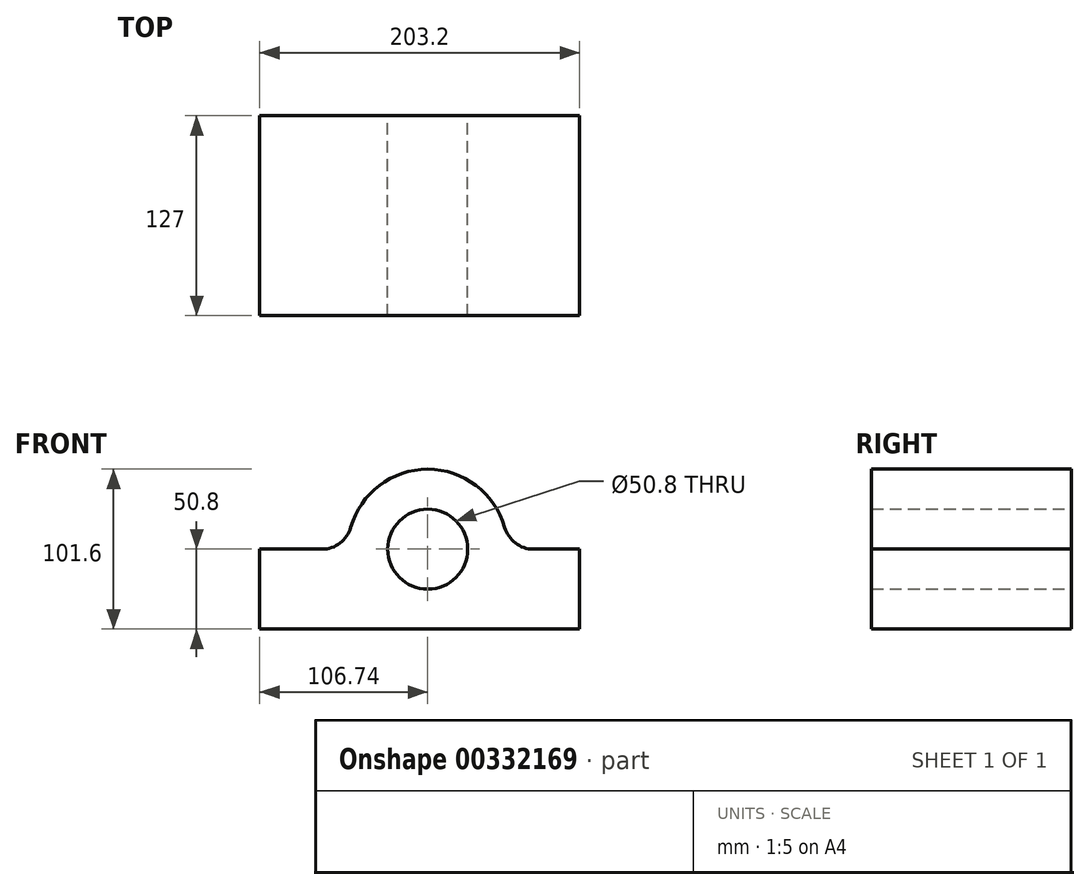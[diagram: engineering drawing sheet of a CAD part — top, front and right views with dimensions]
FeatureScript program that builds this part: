
annotation { "Feature Type Name" : "Feature", "Feature Type Description" : "" }
export const myFeature = defineFeature(function(context is Context, id is Id, definition is map)
    precondition{}
    {
        {
            var Q0;
            Q0=qCreatedBy(makeId("Front.planeOp"),FACE);
            var sketch = newSketch(context, id + "F0", { "sketchPlane" : qUnion([Q0])});
            skCircle(sketch, "E0", {"center": v(0, 0) * mm, "radius": 25.4 * mm});
            skLineSegment(sketch, "E1", {"start": v(96.46, 0) * mm, "end": v(96.46, -50.8) * mm});
            skLineSegment(sketch, "E2", {"start": v(96.46, -50.8) * mm, "end": v(-106.74, -50.8) * mm});
            skLineSegment(sketch, "E3", {"start": v(-106.74, -50.8) * mm, "end": v(-106.74, 0) * mm});
            skLineSegment(sketch, "E4", {"start": v(-106.74, 0) * mm, "end": v(-67.2, 0) * mm});
            skArc(sketch, "E5", {"start": v(48.87, 13.85) * mm, "mid": v(0, 50.8) * mm, "end": v(-48.87, 13.85) * mm});
            skArc(sketch, "E6", {"start": v(-67.2, 0) * mm, "mid": v(-55.71, 3.85) * mm, "end": v(-48.87, 13.85) * mm});
            skArc(sketch, "E7", {"start": v(48.87, 13.85) * mm, "mid": v(55.71, 3.85) * mm, "end": v(67.2, 0) * mm});
            skLineSegment(sketch, "E8.trimOffspring", {"start": v(67.2, 0) * mm, "end": v(96.46, 0) * mm});
            skSolve(sketch);
        }
        {
            var Q0;
            Q0=makeQuery(id+"F0.imprint","IMPRINT",FACE,{"disambiguationData":[TD([[makeQuery(id+"F0.imprint","IMPRINT",EDGE,{"derivedFrom":sQuery(id+"F0.wireOp",EDGE,"E0")}),-1.0]])]});
            extrude(context, id + "F1", {"entities" : qUnion([Q0]), "depth" : 127 * mm});
        }
    });
